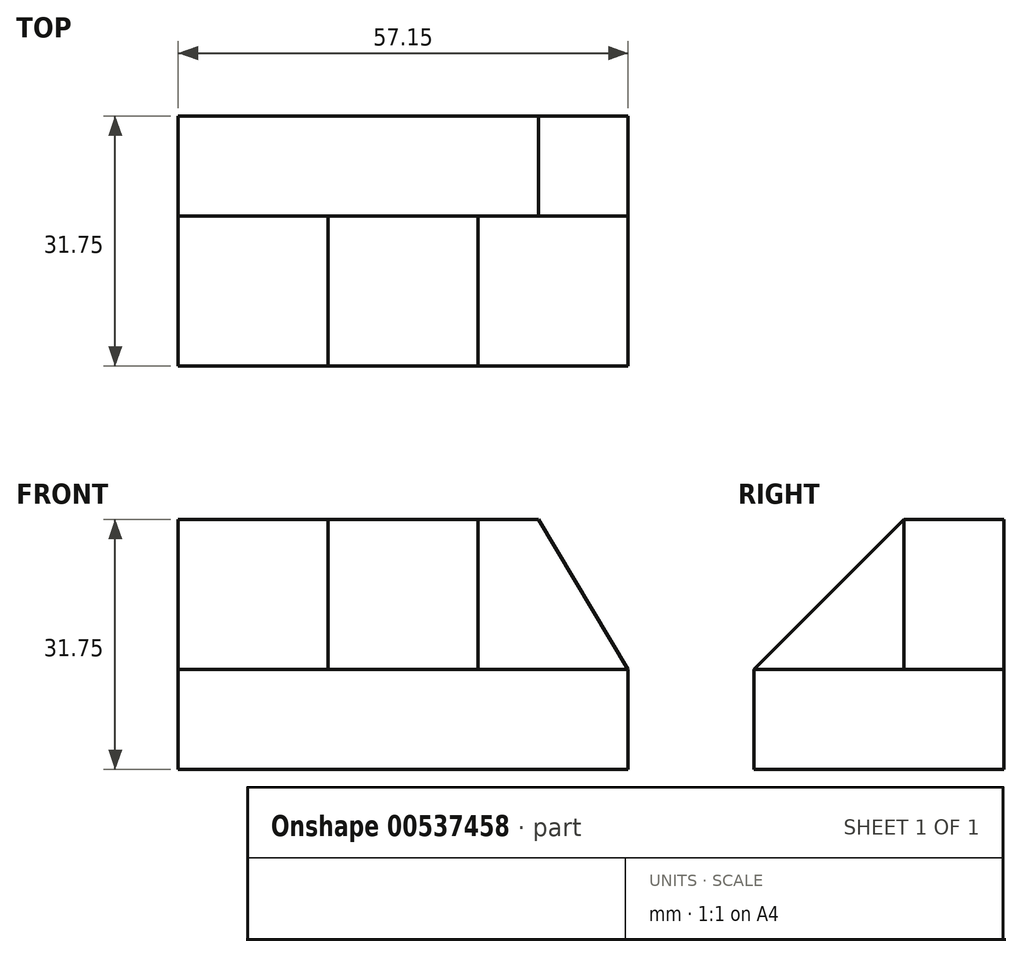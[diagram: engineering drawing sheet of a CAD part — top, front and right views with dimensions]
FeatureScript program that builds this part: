
annotation { "Feature Type Name" : "Feature", "Feature Type Description" : "" }
export const myFeature = defineFeature(function(context is Context, id is Id, definition is map)
    precondition{}
    {
        {
            var Q0;
            Q0=qCreatedBy(makeId("Right.planeOp"),FACE);
            var sketch = newSketch(context, id + "F0", { "sketchPlane" : qUnion([Q0])});
            skLineSegment(sketch, "E0", {"start": v(0, 0) * mm, "end": v(0, 31.75) * mm});
            skLineSegment(sketch, "E1", {"start": v(0, 31.75) * mm, "end": v(-31.75, 31.75) * mm});
            skLineSegment(sketch, "E2", {"start": v(-31.75, 31.75) * mm, "end": v(-31.75, 0) * mm});
            skLineSegment(sketch, "E3", {"start": v(-31.75, 0) * mm, "end": v(0, 0) * mm});
            skSolve(sketch);
        }
        {
            var Q0;
            Q0=makeQuery(id+"F0.imprint","IMPRINT",FACE,{"disambiguationData":[TD([[makeQuery(id+"F0.imprint","IMPRINT",EDGE,{"derivedFrom":sQuery(id+"F0.wireOp",EDGE,"E0")}),1.0]])]});
            extrude(context, id + "F1", {"entities" : qUnion([Q0]), "depth" : 57.15 * mm, "offsetDistance" : 25.4 * mm});
        }
        {
            var Q0;
            Q0=makeQuery(id+"F1.opExtrude","CAP_FACE",FACE,{"disambiguationData":[OSD([sQuery(id+"F0.wireOp",EDGE,"E0"),sQuery(id+"F0.wireOp",EDGE,"E1"),sQuery(id+"F0.wireOp",EDGE,"E2"),sQuery(id+"F0.wireOp",EDGE,"E3")])],"isStart":true});
            var sketch = newSketch(context, id + "F2", { "sketchPlane" : qUnion([Q0])});
            skLineSegment(sketch, "E4", {"start": v(31.75, 12.7) * mm, "end": v(12.7, 12.7) * mm});
            skLineSegment(sketch, "E5", {"start": v(12.7, 12.7) * mm, "end": v(12.7, 31.75) * mm});
            skSolve(sketch);
        }
        {
            var Q0;
            Q0 = qSketchRegion(id + "F2", true);
            var Q1;
            {var subQ0=sQuery(id+"F2.wireOp",EDGE,"E4");Q1=makeQuery(id+"F2.imprint","IMPRINT",FACE,{"disambiguationData":[TD([[makeQuery(id+"F2.imprint","IMPRINT",EDGE,{"derivedFrom":subQ0}),-1.0]])]});}
            extrude(context, id + "F3", {"entities" : qUnion([Q0, Q1]), "operationType" : NewBodyOperationType.REMOVE, "oppositeDirection" : true, "depth" : 19.05 * mm, "offsetDistance" : 25.4 * mm});
        }
        {
            var Q0;
            Q0=makeQuery(id+"F1.opExtrude","CAP_FACE",FACE,{"disambiguationData":[OSD([sQuery(id+"F0.wireOp",EDGE,"E0"),sQuery(id+"F0.wireOp",EDGE,"E1"),sQuery(id+"F0.wireOp",EDGE,"E2"),sQuery(id+"F0.wireOp",EDGE,"E3")])],"isStart":false});
            var sketch = newSketch(context, id + "F4", { "sketchPlane" : qUnion([Q0])});
            skLineSegment(sketch, "E6", {"start": v(-12.7, 31.75) * mm, "end": v(-12.7, 12.7) * mm});
            skLineSegment(sketch, "E7", {"start": v(-12.7, 12.7) * mm, "end": v(-31.75, 12.7) * mm});
            skSolve(sketch);
        }
        {
            var Q0;
            {var subQ0=sQuery(id+"F4.wireOp",EDGE,"E6");Q0=makeQuery(id+"F4.imprint","IMPRINT",FACE,{"disambiguationData":[TD([[makeQuery(id+"F4.imprint","IMPRINT",EDGE,{"derivedFrom":subQ0}),-1.0]])]});}
            extrude(context, id + "F5", {"entities" : qUnion([Q0]), "operationType" : NewBodyOperationType.REMOVE, "oppositeDirection" : true, "depth" : 19.05 * mm, "offsetDistance" : 25.4 * mm});
        }
        {
            var Q0;
            Q0=makeQuery(id+"F5.boolean.opBoolean","COPY",FACE,{"derivedFrom":makeQuery(id+"F5.opExtrude","SWEPT_FACE",FACE,{"disambiguationData":[OSD([sQuery(id+"F4.wireOp",EDGE,"E6")])]})});
            var sketch = newSketch(context, id + "F6", { "sketchPlane" : qUnion([Q0])});
            skLineSegment(sketch, "E8", {"start": v(57.15, 12.7) * mm, "end": v(45.75, 31.75) * mm});
            skSolve(sketch);
        }
        {
            var Q0;
            Q0 = qSketchRegion(id + "F6", true);
            var Q1;
            {var subQ0=sQuery(id+"F6.wireOp",EDGE,"E8");Q1=makeQuery(id+"F6.imprint","IMPRINT",FACE,{"disambiguationData":[TD([[makeQuery(id+"F6.imprint","IMPRINT",EDGE,{"derivedFrom":subQ0}),-1.0]])]});}
            extrude(context, id + "F7", {"entities" : qUnion([Q0, Q1]), "operationType" : NewBodyOperationType.REMOVE, "oppositeDirection" : true, "depth" : 25.4 * mm, "offsetDistance" : 25.4 * mm});
        }
        {
            var Q0;
            Q0=makeQuery(id+"F3.boolean.opBoolean","COPY",FACE,{"derivedFrom":makeQuery(id+"F3.opExtrude","CAP_FACE",FACE,{"disambiguationData":[OSD([sQuery(id+"F0.wireOp",EDGE,"E1"),sQuery(id+"F0.wireOp",EDGE,"E2"),sQuery(id+"F2.wireOp",EDGE,"E4"),sQuery(id+"F2.wireOp",EDGE,"E5")])],"isStart":false})});
            var sketch = newSketch(context, id + "F8", { "sketchPlane" : qUnion([Q0])});
            skLineSegment(sketch, "E9", {"start": v(31.75, 12.7) * mm, "end": v(12.7, 31.75) * mm});
            skSolve(sketch);
        }
        {
            var Q0;
            Q0 = qSketchRegion(id + "F8", true);
            var Q1;
            Q1=makeQuery(id+"F8.imprint","IMPRINT",FACE,{"disambiguationData":[TD([[makeQuery(id+"F8.imprint","IMPRINT",EDGE,{"derivedFrom":sQuery(id+"F8.wireOp",EDGE,"E9")}),-1.0]])]});
            extrude(context, id + "F9", {"entities" : qUnion([Q0, Q1]), "operationType" : NewBodyOperationType.REMOVE, "oppositeDirection" : true, "depth" : 25.4 * mm, "offsetDistance" : 25.4 * mm});
        }
    });
